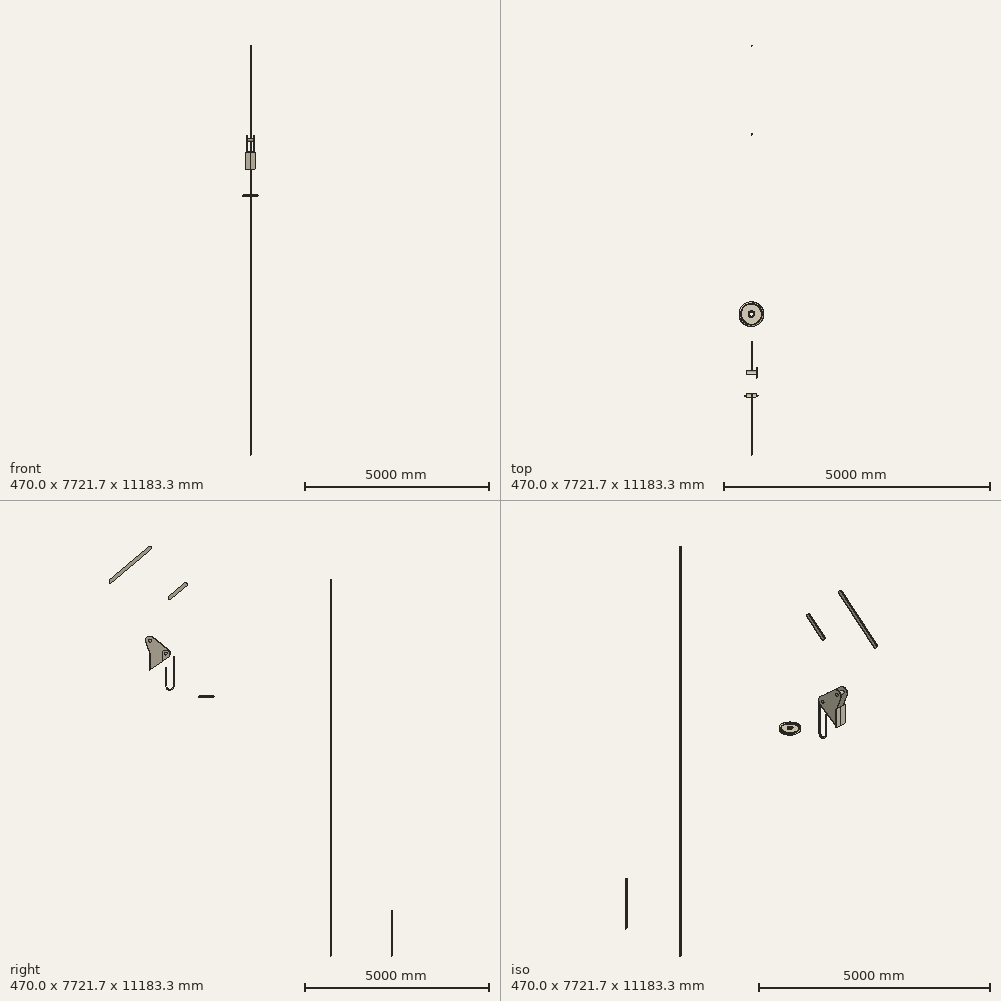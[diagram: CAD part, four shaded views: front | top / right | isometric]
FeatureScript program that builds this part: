
annotation { "Feature Type Name" : "Feature", "Feature Type Description" : "" }
export const myFeature = defineFeature(function(context is Context, id is Id, definition is map)
    precondition{}
    {
        {
            var Q0;
            Q0=qCreatedBy(makeId("Right.planeOp"),FACE);
            var sketch = newSketch(context, id + "F0", { "sketchPlane" : qUnion([Q0])});
            skLineSegment(sketch, "E0", {"start": v(12, 250) * mm, "end": v(12, -200) * mm});
            skCircle(sketch, "E1", {"center": v(445.01, 250) * mm, "radius": 125 * mm});
            skCircle(sketch, "E2", {"center": v(12, 600) * mm, "radius": 125 * mm});
            skLineSegment(sketch, "E3", {"start": v(12, 600) * mm, "end": v(445.01, 250) * mm, "construction": true});
            skLineSegment(sketch, "E4", {"start": v(12, 250) * mm, "end": v(445.01, 250) * mm, "construction": true});
            skLineSegment(sketch, "E5", {"start": v(12, 250) * mm, "end": v(12, 600) * mm, "construction": true});
            skCircle(sketch, "E6", {"center": v(12, 600) * mm, "radius": 40 * mm});
            skCircle(sketch, "E7", {"center": v(445.01, 250) * mm, "radius": 40 * mm});
            skLineSegment(sketch, "E8", {"start": v(90.58, 697.21) * mm, "end": v(523.6, 347.21) * mm});
            skLineSegment(sketch, "E9", {"start": v(12, 250) * mm, "end": v(-104.76, 555.36) * mm});
            skLineSegment(sketch, "E10", {"start": v(12, -200) * mm, "end": v(515.91, 147.05) * mm});
            skLineSegment(sketch, "E11", {"start": v(12, 250) * mm, "end": v(0, 250) * mm});
            skLineSegment(sketch, "E12", {"start": v(0, 250) * mm, "end": v(0, -200) * mm});
            skLineSegment(sketch, "E13", {"start": v(0, -200) * mm, "end": v(12, -200) * mm});
            skLineSegment(sketch, "E14", {"start": v(-46.5, 403.02) * mm, "end": v(85.45, 498.86) * mm, "construction": true});
            skLineSegment(sketch, "E15", {"start": v(85.45, 498.86) * mm, "end": v(217.41, 594.7) * mm, "construction": true});
            skLineSegment(sketch, "E16", {"start": v(320.01, 250) * mm, "end": v(320.01, 511.76) * mm, "construction": true});
            skLineSegment(sketch, "E17", {"start": v(320.01, 250) * mm, "end": v(320.01, 12.13) * mm, "construction": true});
            skLineSegment(sketch, "E18", {"start": v(0, 250) * mm, "end": v(0, 262) * mm});
            skLineSegment(sketch, "E19", {"start": v(0, 262) * mm, "end": v(12, 250) * mm});
            skLineSegment(sketch, "E20", {"start": v(0, -200) * mm, "end": v(0, -212) * mm});
            skLineSegment(sketch, "E21", {"start": v(0, -212) * mm, "end": v(12, -200) * mm});
            skSolve(sketch);
        }
        {
            var Q0;
            Q0=makeQuery(id+"F0.imprint","IMPRINT",FACE,{"disambiguationData":[TD([[makeQuery(id+"F0.imprint","IMPRINT",EDGE,{"derivedFrom":sQuery(id+"F0.wireOp",EDGE,"E0")}),-1.0]])]});
            var Q1;
            Q1=makeQuery(id+"F0.imprint","IMPRINT",FACE,{"disambiguationData":[TD([[makeQuery(id+"F0.imprint","IMPRINT",EDGE,{"derivedFrom":sQuery(id+"F0.wireOp",EDGE,"E11")}),-1.0]])]});
            var Q2;
            Q2=makeQuery(id+"F0.imprint","IMPRINT",FACE,{"disambiguationData":[TD([[makeQuery(id+"F0.imprint","IMPRINT",EDGE,{"derivedFrom":sQuery(id+"F0.wireOp",EDGE,"E13")}),-1.0]])]});
            extrude(context, id + "F1", {"entities" : qUnion([Q0, Q1, Q2]), "depth" : (250 + 22) * mm / 2});
        }
        {
            var Q0;
            Q0=makeQuery(id+"F0.imprint","IMPRINT",FACE,{"disambiguationData":[TD([[makeQuery(id+"F0.imprint","IMPRINT",EDGE,{"derivedFrom":sQuery(id+"F0.wireOp",EDGE,"E0")}),1.0]])]});
            var Q1;
            Q1=makeQuery(id+"F0.imprint","IMPRINT",FACE,{"disambiguationData":[TD([[makeQuery(id+"F0.imprint","IMPRINT",EDGE,{"derivedFrom":sQuery(id+"F0.wireOp",EDGE,"E6")}),-1.0]])]});
            var Q2;
            Q2=makeQuery(id+"F0.imprint","IMPRINT",FACE,{"disambiguationData":[TD([[makeQuery(id+"F0.imprint","IMPRINT",EDGE,{"derivedFrom":sQuery(id+"F0.wireOp",EDGE,"E7")}),-1.0]])]});
            extrude(context, id + "F2", {"entities" : qUnion([Q0, Q1, Q2]), "depth" : (12 + 90) * mm, "hasSecondDirection" : true, "secondDirectionOppositeDirection" : false, "secondDirectionDepth" : 90 * mm});
        }
        {
            var Q0;
            Q0=makeQuery(id+"F1.opExtrude","SWEPT_BODY",BODY,{"disambiguationData":[OSD([sQuery(id+"F0.wireOp",EDGE,"E0"),sQuery(id+"F0.wireOp",EDGE,"E11"),sQuery(id+"F0.wireOp",EDGE,"E12"),sQuery(id+"F0.wireOp",EDGE,"E13")])]});
            var Q1;
            Q1=makeQuery(id+"F2.opExtrude","SWEPT_BODY",BODY,{"disambiguationData":[OSD([sQuery(id+"F0.wireOp",EDGE,"E0"),sQuery(id+"F0.wireOp",EDGE,"E1"),sQuery(id+"F0.wireOp",EDGE,"E2"),sQuery(id+"F0.wireOp",EDGE,"E6"),sQuery(id+"F0.wireOp",EDGE,"E7"),sQuery(id+"F0.wireOp",EDGE,"E8"),sQuery(id+"F0.wireOp",EDGE,"E9"),sQuery(id+"F0.wireOp",EDGE,"E10"),sQuery(id+"F0.wireOp",EDGE,"E11")])]});
            var Q2;
            Q2=qCreatedBy(makeId("Right.planeOp"),FACE);
            mirror(context, id + "F3", {"entities" : qUnion([Q0, Q1]), "mirrorPlane" : qUnion([Q2])});
        }
        {
            var Q0;
            Q0=makeQuery(id+"F0.imprint","IMPRINT",FACE,{"disambiguationData":[TD([[makeQuery(id+"F0.imprint","IMPRINT",EDGE,{"derivedFrom":sQuery(id+"F0.wireOp",EDGE,"E7")}),1.0]])]});
            var Q1;
            Q1=makeQuery(id+"F0.imprint","IMPRINT",FACE,{"disambiguationData":[TD([[makeQuery(id+"F0.imprint","IMPRINT",EDGE,{"derivedFrom":sQuery(id+"F0.wireOp",EDGE,"E6")}),1.0]])]});
            var Q2;
            Q2=makeQuery(id+"F2.opExtrude","CAP_FACE",FACE,{"disambiguationData":[OSD([sQuery(id+"F0.wireOp",EDGE,"E0"),sQuery(id+"F0.wireOp",EDGE,"E1"),sQuery(id+"F0.wireOp",EDGE,"E2"),sQuery(id+"F0.wireOp",EDGE,"E6"),sQuery(id+"F0.wireOp",EDGE,"E7"),sQuery(id+"F0.wireOp",EDGE,"E8"),sQuery(id+"F0.wireOp",EDGE,"E9"),sQuery(id+"F0.wireOp",EDGE,"E10")])],"isStart":false});
            var Q3;
            Q3=makeQuery(id+"F3.opPattern","COPY",FACE,{"derivedFrom":makeQuery(id+"F2.opExtrude","CAP_FACE",FACE,{"disambiguationData":[OSD([sQuery(id+"F0.wireOp",EDGE,"E0"),sQuery(id+"F0.wireOp",EDGE,"E1"),sQuery(id+"F0.wireOp",EDGE,"E2"),sQuery(id+"F0.wireOp",EDGE,"E6"),sQuery(id+"F0.wireOp",EDGE,"E7"),sQuery(id+"F0.wireOp",EDGE,"E8"),sQuery(id+"F0.wireOp",EDGE,"E9"),sQuery(id+"F0.wireOp",EDGE,"E10")])],"isStart":false}),"instanceName":"1"});
            extrude(context, id + "F4", {"entities" : qUnion([Q0, Q1]), "endBound" : BoundingType.UP_TO_SURFACE, "endBoundEntityFace" : qUnion([Q2]), "depth" : 25 * mm, "hasSecondDirection" : true, "secondDirectionBound" : SecondDirectionBoundingType.UP_TO_SURFACE, "secondDirectionOppositeDirection" : true, "secondDirectionBoundEntityFace" : qUnion([Q3]), "secondDirectionDepth" : 25 * mm});
        }
        {
            var Q0;
            Q0=qCreatedBy(makeId("Right.planeOp"),FACE);
            var sketch = newSketch(context, id + "F5", { "sketchPlane" : qUnion([Q0])});
            skLineSegment(sketch, "E22", {"start": v(550.8, 1767.91) * mm, "end": v(986.47, 2135.46) * mm, "construction": true});
            skArc(sketch, "E23", {"start": v(518.57, 1806.13) * mm, "mid": v(512.6, 1735.67) * mm, "end": v(583.05, 1729.7) * mm});
            skArc(sketch, "E24", {"start": v(1018.72, 2097.25) * mm, "mid": v(1024.7, 2167.7) * mm, "end": v(954.23, 2173.68) * mm});
            skLineSegment(sketch, "E25.0", {"start": v(583.05, 1729.7) * mm, "end": v(1018.72, 2097.25) * mm});
            skLineSegment(sketch, "E26.0", {"start": v(518.57, 1806.13) * mm, "end": v(954.23, 2173.68) * mm});
            skLineSegment(sketch, "E27", {"start": v(954.23, 2173.68) * mm, "end": v(1018.72, 2097.25) * mm, "construction": true});
            skSolve(sketch);
        }
        {
            var Q0;
            Q0 = qSketchRegion(id + "F5", true);
            extrude(context, id + "F6", {"entities" : qUnion([Q0]), "depth" : 25 * mm});
        }
        {
            var Q0;
            Q0=qCreatedBy(makeId("Right.planeOp"),FACE);
            var sketch = newSketch(context, id + "F7", { "sketchPlane" : qUnion([Q0])});
            skLineSegment(sketch, "E28", {"start": v(1588.17, -878.89) * mm, "end": v(1588.17, -938.89) * mm});
            skLineSegment(sketch, "E29", {"start": v(1588.17, -908.89) * mm, "end": v(1748.17, -908.89) * mm});
            skLineSegment(sketch, "E30", {"start": v(1588.17, -908.89) * mm, "end": v(1548.17, -908.89) * mm, "construction": true});
            skLineSegment(sketch, "E31", {"start": v(1748.17, -908.89) * mm, "end": v(1783.17, -908.89) * mm, "construction": true});
            skArc(sketch, "E32", {"start": v(1748.17, -908.89) * mm, "mid": v(1749.8, -914.65) * mm, "end": v(1754.2, -918.7) * mm});
            skLineSegment(sketch, "E33", {"start": v(1548.17, -908.89) * mm, "end": v(1548.17, -938.89) * mm, "construction": true});
            skLineSegment(sketch, "E34", {"start": v(1783.17, -938.89) * mm, "end": v(1783.17, -933.39) * mm});
            skLineSegment(sketch, "E35", {"start": v(1783.17, -933.39) * mm, "end": v(1754.2, -918.7) * mm});
            skArc(sketch, "E36", {"start": v(1745.97, -918.79) * mm, "mid": v(1748.57, -921.53) * mm, "end": v(1751.71, -923.6) * mm});
            skLineSegment(sketch, "E37", {"start": v(1781.86, -938.89) * mm, "end": v(1751.71, -923.6) * mm});
            skLineSegment(sketch, "E38", {"start": v(1613.32, -914.39) * mm, "end": v(1737.17, -914.39) * mm});
            skLineSegment(sketch, "E39.trimOffspring", {"start": v(1781.86, -938.89) * mm, "end": v(1783.17, -938.89) * mm});
            skLineSegment(sketch, "E40", {"start": v(1588.17, -938.89) * mm, "end": v(1599.17, -938.89) * mm});
            skLineSegment(sketch, "E41", {"start": v(1599.17, -938.89) * mm, "end": v(1613.32, -914.39) * mm});
            skPoint(sketch, "E42.visualSharp", {"position": v(1743.62, -914.39) * mm});
            skArc(sketch, "E42.filletArc", {"start": v(1745.97, -918.79) * mm, "mid": v(1742.1, -915.55) * mm, "end": v(1737.17, -914.39) * mm});
            skSolve(sketch);
        }
        {
            var Q0;
            {var subQ2=sQuery(id+"F7.wireOp",EDGE,"E29");Q0=makeQuery(id+"F7.imprint","IMPRINT",FACE,{"disambiguationData":[TD([[makeQuery(id+"F7.imprint","IMPRINT",EDGE,{"derivedFrom":subQ2}),-1.0]])]});}
            var Q1;
            Q1=sQuery(id+"F7.wireOp",EDGE,"E33");
            revolve(context, id + "F8", {"entities" : qUnion([Q0]), "axis" : qUnion([Q1]), "revolveType" : RevolveType.FULL});
        }
        {
            var Q0;
            Q0=makeQuery(id+"F8.opRevolve","SWEPT_BODY",BODY,{"disambiguationData":[OSD([sQuery(id+"F7.wireOp",EDGE,"E28"),sQuery(id+"F7.wireOp",EDGE,"E29"),sQuery(id+"F7.wireOp",EDGE,"E32"),sQuery(id+"F7.wireOp",EDGE,"E34"),sQuery(id+"F7.wireOp",EDGE,"E35"),sQuery(id+"F7.wireOp",EDGE,"E36"),sQuery(id+"F7.wireOp",EDGE,"E37"),sQuery(id+"F7.wireOp",EDGE,"E38"),sQuery(id+"F7.wireOp",EDGE,"E39.trimOffspring"),sQuery(id+"F7.wireOp",EDGE,"E40"),sQuery(id+"F7.wireOp",EDGE,"E41"),sQuery(id+"F7.wireOp",EDGE,"E42.filletArc")])]});
            var Q1;
            Q1=makeQuery(id+"F8.opRevolve","SWEPT_FACE",FACE,{"disambiguationData":[OSD([sQuery(id+"F7.wireOp",EDGE,"E29")])]});
            mirror(context, id + "F9", {"operationType" : NewBodyOperationType.ADD, "entities" : qUnion([Q0]), "mirrorPlane" : qUnion([Q1])});
        }
        {
            var Q0;
            Q0=qCreatedBy(makeId("Right.planeOp"),FACE);
            var sketch = newSketch(context, id + "F10", { "sketchPlane" : qUnion([Q0])});
            skLineSegment(sketch, "E43", {"start": v(-1061.08, 2221.36) * mm, "end": v(8.98, 3124.12) * mm, "construction": true});
            skArc(sketch, "E44", {"start": v(-1093.32, 2259.58) * mm, "mid": v(-1099.3, 2189.12) * mm, "end": v(-1028.84, 2183.15) * mm});
            skArc(sketch, "E45", {"start": v(41.22, 3085.9) * mm, "mid": v(47.2, 3156.36) * mm, "end": v(-23.26, 3162.33) * mm});
            skLineSegment(sketch, "E46.0", {"start": v(-1028.84, 2183.15) * mm, "end": v(41.22, 3085.9) * mm});
            skLineSegment(sketch, "E47.0", {"start": v(-1093.32, 2259.58) * mm, "end": v(-23.26, 3162.33) * mm});
            skLineSegment(sketch, "E48", {"start": v(-23.26, 3162.33) * mm, "end": v(41.22, 3085.9) * mm, "construction": true});
            skSolve(sketch);
        }
        {
            var Q0;
            Q0=makeQuery(id+"F10.imprint","IMPRINT",FACE,{"disambiguationData":[TD([[makeQuery(id+"F10.imprint","IMPRINT",EDGE,{"derivedFrom":sQuery(id+"F10.wireOp",EDGE,"E44")}),1.0]])]});
            extrude(context, id + "F11", {"entities" : qUnion([Q0]), "depth" : 25 * mm});
        }
        {
            var Q0;
            Q0=makeQuery(id+"F2.opExtrude","CAP_FACE",FACE,{"disambiguationData":[OSD([sQuery(id+"F0.wireOp",EDGE,"E0"),sQuery(id+"F0.wireOp",EDGE,"E1"),sQuery(id+"F0.wireOp",EDGE,"E2"),sQuery(id+"F0.wireOp",EDGE,"E6"),sQuery(id+"F0.wireOp",EDGE,"E7"),sQuery(id+"F0.wireOp",EDGE,"E8"),sQuery(id+"F0.wireOp",EDGE,"E9"),sQuery(id+"F0.wireOp",EDGE,"E10")])],"isStart":false});
            var sketch = newSketch(context, id + "F12", { "sketchPlane" : qUnion([Q0])});
            skCircle(sketch, "E49.0", {"center": v(445.01, 250) * mm, "radius": 40 * mm});
            skLineSegment(sketch, "E50", {"start": v(445.01, 250) * mm, "end": v(445.01, -100) * mm});
            skArc(sketch, "E51.0.startCap", {"start": v(345.01, 250) * mm, "mid": v(445.01, 350) * mm, "end": v(545.01, 250) * mm});
            skArc(sketch, "E51.0.endCap", {"start": v(545.01, -100) * mm, "mid": v(445.01, -200) * mm, "end": v(345.01, -100) * mm});
            skLineSegment(sketch, "E51.0.left", {"start": v(545.01, 250) * mm, "end": v(545.01, -100) * mm});
            skLineSegment(sketch, "E51.0.right", {"start": v(345.01, 250) * mm, "end": v(345.01, -100) * mm});
            skCircle(sketch, "E52", {"center": v(445.01, -100) * mm, "radius": 40 * mm});
            skSolve(sketch);
        }
        {
            var Q0;
            Q0=makeQuery(id+"F12.imprint","IMPRINT",FACE,{"disambiguationData":[TD([[makeQuery(id+"F12.imprint","IMPRINT",EDGE,{"derivedFrom":sQuery(id+"F12.wireOp",EDGE,"E49.0")}),-1.0]])]});
            var Q1;
            {var subQ1=sQuery(id+"F12.wireOp",EDGE,"E51.0.endCap");Q1=makeQuery(id+"F12.imprint","IMPRINT",FACE,{"disambiguationData":[TD([[makeQuery(id+"F12.imprint","IMPRINT",EDGE,{"derivedFrom":subQ1}),-1.0]])]});}
            extrude(context, id + "F13", {"entities" : qUnion([Q0, Q1]), "depth" : 10 * mm, "offsetDistance" : 25 * mm});
        }
        {
            var Q0;
            Q0=qCreatedBy(makeId("Right.planeOp"),FACE);
            var sketch = newSketch(context, id + "F14", { "sketchPlane" : qUnion([Q0])});
            skLineSegment(sketch, "E53", {"start": v(456.58, -138.87) * mm, "end": v(456.58, -638.87) * mm});
            skLineSegment(sketch, "E54", {"start": v(656.58, 161.13) * mm, "end": v(656.58, -638.87) * mm});
            skArc(sketch, "E55", {"start": v(456.58, -638.87) * mm, "mid": v(556.58, -738.87) * mm, "end": v(656.58, -638.87) * mm});
            skArc(sketch, "E56.0.startCap", {"start": v(444.08, -638.87) * mm, "mid": v(456.58, -626.37) * mm, "end": v(469.08, -638.87) * mm});
            skArc(sketch, "E56.0.endCap", {"start": v(644.08, -638.87) * mm, "mid": v(656.58, -626.37) * mm, "end": v(669.08, -638.87) * mm});
            skArc(sketch, "E56.0.left", {"start": v(469.08, -638.87) * mm, "mid": v(556.58, -726.37) * mm, "end": v(644.08, -638.87) * mm});
            skArc(sketch, "E56.0.right", {"start": v(444.08, -638.87) * mm, "mid": v(556.58, -751.37) * mm, "end": v(669.08, -638.87) * mm});
            skArc(sketch, "E56.1.startCap", {"start": v(644.08, 161.13) * mm, "mid": v(656.58, 173.63) * mm, "end": v(669.08, 161.13) * mm});
            skArc(sketch, "E56.1.endCap", {"start": v(669.08, -638.87) * mm, "mid": v(656.58, -651.37) * mm, "end": v(644.08, -638.87) * mm});
            skLineSegment(sketch, "E56.1.left", {"start": v(669.08, 161.13) * mm, "end": v(669.08, -638.87) * mm});
            skLineSegment(sketch, "E56.1.right", {"start": v(644.08, 161.13) * mm, "end": v(644.08, -638.87) * mm});
            skArc(sketch, "E56.2.startCap", {"start": v(444.08, -138.87) * mm, "mid": v(456.58, -126.37) * mm, "end": v(469.08, -138.87) * mm});
            skArc(sketch, "E56.2.endCap", {"start": v(469.08, -638.87) * mm, "mid": v(456.58, -651.37) * mm, "end": v(444.08, -638.87) * mm});
            skLineSegment(sketch, "E56.2.left", {"start": v(469.08, -138.87) * mm, "end": v(469.08, -638.87) * mm});
            skLineSegment(sketch, "E56.2.right", {"start": v(444.08, -138.87) * mm, "end": v(444.08, -638.87) * mm});
            skSolve(sketch);
        }
        {
            var Q0;
            Q0 = qSketchRegion(id + "F14", true);
            extrude(context, id + "F15", {"entities" : qUnion([Q0]), "depth" : 25 * mm, "offsetDistance" : 25 * mm});
        }
        {
            var Q0;
            Q0=qCreatedBy(makeId("Right.planeOp"),FACE);
            var sketch = newSketch(context, id + "F16", { "sketchPlane" : qUnion([Q0])});
            skLineSegment(sketch, "E57", {"start": v(4935.62, -7996.67) * mm, "end": v(4935.62, 2253.33) * mm});
            skArc(sketch, "E58.0.startCap", {"start": v(4948.12, -7996.67) * mm, "mid": v(4935.62, -8009.17) * mm, "end": v(4923.12, -7996.67) * mm});
            skArc(sketch, "E58.0.endCap", {"start": v(4923.12, 2253.33) * mm, "mid": v(4935.62, 2265.83) * mm, "end": v(4948.12, 2253.33) * mm});
            skLineSegment(sketch, "E58.0.left", {"start": v(4923.12, -7996.67) * mm, "end": v(4923.12, 2253.33) * mm});
            skLineSegment(sketch, "E58.0.right", {"start": v(4948.12, -7996.67) * mm, "end": v(4948.12, 2253.33) * mm});
            skLineSegment(sketch, "E59", {"start": v(6598.12, -7996.67) * mm, "end": v(6598.12, -6746.67) * mm});
            skArc(sketch, "E60.0.startCap", {"start": v(6610.62, -7996.67) * mm, "mid": v(6598.12, -8009.17) * mm, "end": v(6585.62, -7996.67) * mm});
            skArc(sketch, "E60.0.endCap", {"start": v(6585.62, -6746.67) * mm, "mid": v(6598.12, -6734.17) * mm, "end": v(6610.62, -6746.67) * mm});
            skLineSegment(sketch, "E60.0.left", {"start": v(6585.62, -7996.67) * mm, "end": v(6585.62, -6746.67) * mm});
            skLineSegment(sketch, "E60.0.right", {"start": v(6610.62, -7996.67) * mm, "end": v(6610.62, -6746.67) * mm});
            skSolve(sketch);
        }
        {
            var Q0;
            Q0 = qSketchRegion(id + "F16", true);
            extrude(context, id + "F17", {"entities" : qUnion([Q0]), "depth" : 25 * mm, "offsetDistance" : 25 * mm});
        }
        {
            var Q0;
            Q0 = qConstructionFilter(qBodyType(qCreatedBy(id + "F16" ,EDGE), BodyType.WIRE), ConstructionObject.NO);
            extrude(context, id + "F18", {"bodyType" : ToolBodyType.SURFACE, "surfaceEntities" : qUnion([Q0]), "depth" : 25 * mm, "offsetDistance" : 25 * mm});
        }
    });
